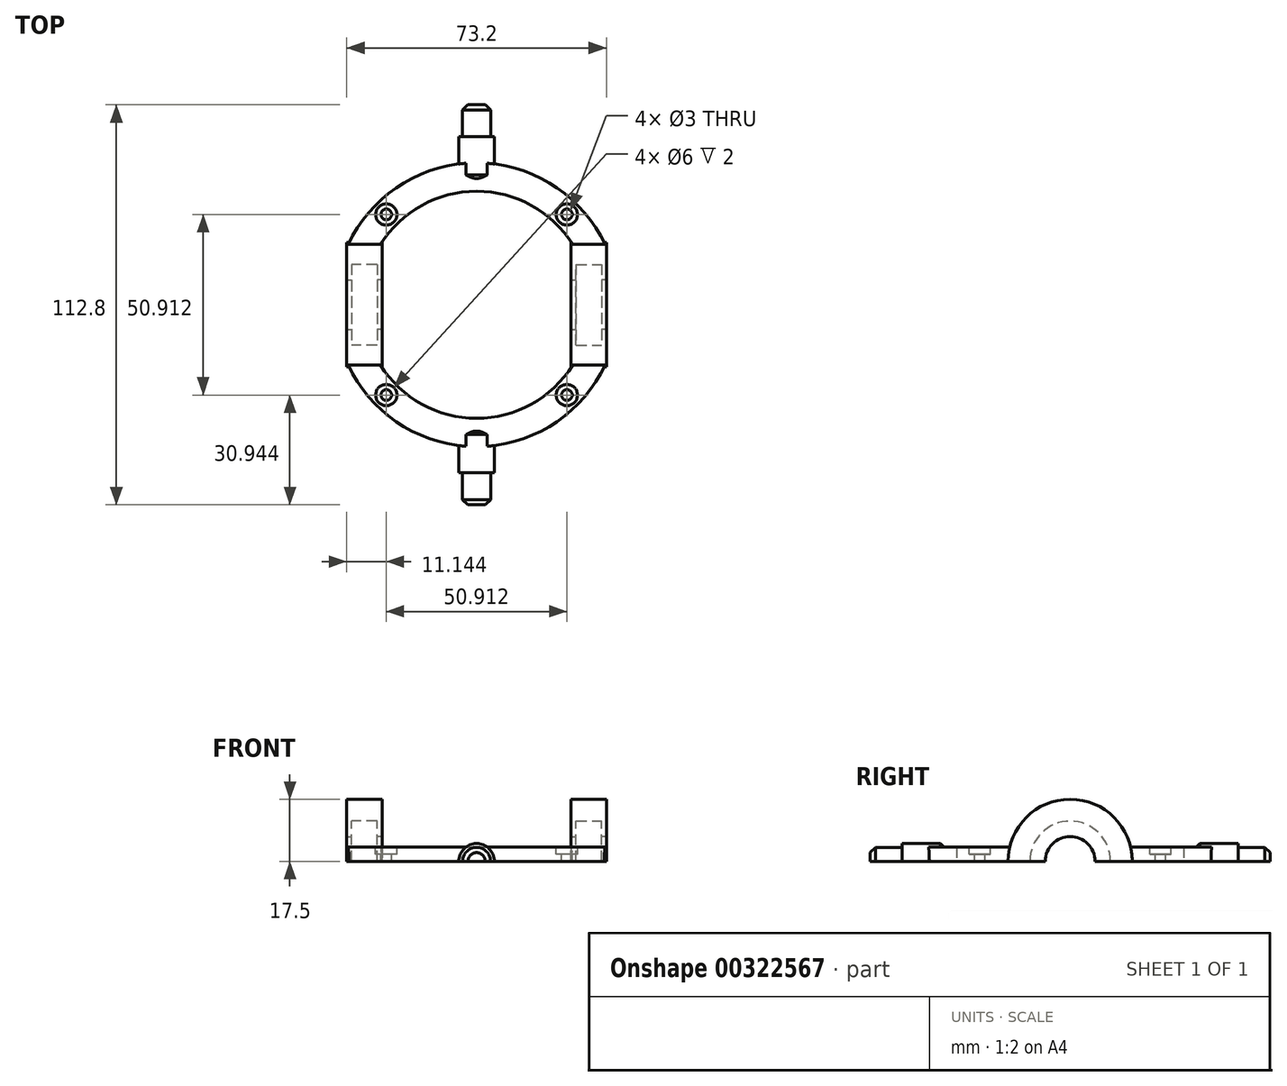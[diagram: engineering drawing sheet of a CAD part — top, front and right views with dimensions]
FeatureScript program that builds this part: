
annotation { "Feature Type Name" : "Feature", "Feature Type Description" : "" }
export const myFeature = defineFeature(function(context is Context, id is Id, definition is map)
    precondition{}
    {
        {
            var Q0;
            Q0=qCreatedBy(makeId("Top.planeOp"),FACE);
            var sketch = newSketch(context, id + "F0", { "sketchPlane" : qUnion([Q0])});
            skCircle(sketch, "E0", {"center": v(0, 0) * mm, "radius": 50 * mm});
            skCircle(sketch, "E1", {"center": v(0, 0) * mm, "radius": 58 * mm});
            skSolve(sketch);
        }
        {
            var Q0;
            Q0=qSketchRegion(id+"F0",true);
            extrude(context, id + "F1", {"entities" : qUnion([Q0]), "depth" : 4 * mm, "hasSecondDirection" : true, "secondDirectionOppositeDirection" : true, "secondDirectionDepth" : 4 * mm});
        }
        {
            var Q0;
            Q0=qCreatedBy(makeId("Front.planeOp"),FACE);
            cPlane(context, id + "F2", {"entities" : qUnion([Q0]), "cplaneType" : CPlaneType.OFFSET, "offset" : 54.8 * mm, "width" : 150 * mm, "height" : 150 * mm});
        }
        {
            var Q0;
            Q0=qCreatedBy(id+"F2.planeOp",FACE);
            var sketch = newSketch(context, id + "F3", { "sketchPlane" : qUnion([Q0])});
            skCircle(sketch, "E2", {"center": v(0, 0) * mm, "radius": 11.35 * mm});
            skCircle(sketch, "E3", {"center": v(0, 0) * mm, "radius": 17.5 * mm});
            skSolve(sketch);
        }
        {
            var Q0;
            Q0=makeQuery(id+"F3.imprint","IMPRINT",FACE,{"disambiguationData":[TD([[makeQuery(id+"F3.imprint","IMPRINT",EDGE,{"derivedFrom":sQuery(id+"F3.wireOp",EDGE,"E2")}),1.0]])]});
            var Q1;
            Q1=makeQuery(id+"F3.imprint","IMPRINT",FACE,{"disambiguationData":[TD([[makeQuery(id+"F3.imprint","IMPRINT",EDGE,{"derivedFrom":sQuery(id+"F3.wireOp",EDGE,"E2")}),-1.0]])]});
            extrude(context, id + "F4", {"entities" : qUnion([Q0, Q1]), "operationType" : NewBodyOperationType.REMOVE, "oppositeDirection" : true, "depth" : 25 * mm, "hasSecondDirection" : true, "secondDirectionOppositeDirection" : false, "secondDirectionDepth" : 25 * mm});
        }
        {
            var Q0;
            Q0=makeQuery(id+"F3.imprint","IMPRINT",FACE,{"disambiguationData":[TD([[makeQuery(id+"F3.imprint","IMPRINT",EDGE,{"derivedFrom":sQuery(id+"F3.wireOp",EDGE,"E2")}),-1.0]])]});
            extrude(context, id + "F5", {"entities" : qUnion([Q0]), "operationType" : NewBodyOperationType.ADD, "oppositeDirection" : true, "depth" : 7.2 * mm});
        }
        {
            var Q0;
            Q0=makeQuery(id+"F5.opExtrude","CAP_FACE",FACE,{"disambiguationData":[OSD([sQuery(id+"F3.wireOp",EDGE,"E2"),sQuery(id+"F3.wireOp",EDGE,"E3")])],"isStart":true});
            var sketch = newSketch(context, id + "F6", { "sketchPlane" : qUnion([Q0])});
            skCircle(sketch, "E4", {"center": v(0, 0) * mm, "radius": 7 * mm});
            skCircle(sketch, "E5", {"center": v(0, 0) * mm, "radius": 17.5 * mm});
            skSolve(sketch);
        }
        {
            var Q0;
            Q0=makeQuery(id+"F6.imprint","IMPRINT",FACE,{"disambiguationData":[TD([[makeQuery(id+"F6.imprint","IMPRINT",EDGE,{"derivedFrom":sQuery(id+"F6.wireOp",EDGE,"E4")}),-1.0]])]});
            var Q1;
            Q1=makeQuery(id+"F6.imprint","IMPRINT",FACE,{"disambiguationData":[TD([[makeQuery(id+"F6.imprint","IMPRINT",EDGE,{"derivedFrom":sQuery(id+"F6.wireOp",EDGE,"E5")}),1.0]])]});
            extrude(context, id + "F7", {"entities" : qUnion([Q0, Q1]), "operationType" : NewBodyOperationType.ADD, "depth" : 1.4 * mm});
        }
        {
            var Q0;
            Q0=makeQuery(id+"F5.opExtrude","CAP_FACE",FACE,{"disambiguationData":[OSD([sQuery(id+"F3.wireOp",EDGE,"E2"),sQuery(id+"F3.wireOp",EDGE,"E3")])],"isStart":false});
            var sketch = newSketch(context, id + "F8", { "sketchPlane" : qUnion([Q0])});
            skCircle(sketch, "E6", {"center": v(0, 0) * mm, "radius": 7 * mm});
            skCircle(sketch, "E7", {"center": v(0, 0) * mm, "radius": 17.5 * mm});
            skSolve(sketch);
        }
        {
            var Q0;
            Q0=makeQuery(id+"F8.imprint","IMPRINT",FACE,{"disambiguationData":[TD([[makeQuery(id+"F8.imprint","IMPRINT",EDGE,{"derivedFrom":sQuery(id+"F8.wireOp",EDGE,"E7")}),-1.0]])]});
            var Q1;
            Q1=makeQuery(id+"F8.imprint","IMPRINT",FACE,{"disambiguationData":[TD([[makeQuery(id+"F8.imprint","IMPRINT",EDGE,{"derivedFrom":sQuery(id+"F8.wireOp",EDGE,"E6")}),-1.0]])]});
            extrude(context, id + "F9", {"entities" : qUnion([Q0, Q1]), "operationType" : NewBodyOperationType.ADD, "depth" : 1.4 * mm});
        }
        {
            var Q0;
            Q0=qCreatedBy(makeId("Front.planeOp"),FACE);
            cPlane(context, id + "F10", {"entities" : qUnion([Q0]), "cplaneType" : CPlaneType.OFFSET, "offset" : 54.8 * mm, "oppositeDirection" : true, "width" : 150 * mm, "height" : 150 * mm});
        }
        {
            var Q0;
            Q0=qCreatedBy(id+"F10.planeOp",FACE);
            var sketch = newSketch(context, id + "F11", { "sketchPlane" : qUnion([Q0])});
            skCircle(sketch, "E8", {"center": v(0, 0) * mm, "radius": 17.5 * mm});
            skCircle(sketch, "E9", {"center": v(0, 0) * mm, "radius": 11.35 * mm});
            skSolve(sketch);
        }
        {
            var Q0;
            Q0=makeQuery(id+"F11.imprint","IMPRINT",FACE,{"disambiguationData":[TD([[makeQuery(id+"F11.imprint","IMPRINT",EDGE,{"derivedFrom":sQuery(id+"F11.wireOp",EDGE,"E8")}),1.0]])]});
            var Q1;
            Q1=makeQuery(id+"F11.imprint","IMPRINT",FACE,{"disambiguationData":[TD([[makeQuery(id+"F11.imprint","IMPRINT",EDGE,{"derivedFrom":sQuery(id+"F11.wireOp",EDGE,"E9")}),1.0]])]});
            extrude(context, id + "F12", {"entities" : qUnion([Q0, Q1]), "operationType" : NewBodyOperationType.REMOVE, "depth" : 25 * mm, "hasSecondDirection" : true, "secondDirectionOppositeDirection" : true, "secondDirectionDepth" : 25 * mm});
        }
        {
            var Q0;
            Q0=makeQuery(id+"F11.imprint","IMPRINT",FACE,{"disambiguationData":[TD([[makeQuery(id+"F11.imprint","IMPRINT",EDGE,{"derivedFrom":sQuery(id+"F11.wireOp",EDGE,"E8")}),1.0]])]});
            extrude(context, id + "F13", {"entities" : qUnion([Q0]), "operationType" : NewBodyOperationType.ADD, "depth" : 7.2 * mm});
        }
        {
            var Q0;
            Q0=makeQuery(id+"F13.opExtrude","CAP_FACE",FACE,{"disambiguationData":[OSD([sQuery(id+"F11.wireOp",EDGE,"E8"),sQuery(id+"F11.wireOp",EDGE,"E9")])],"isStart":true});
            var sketch = newSketch(context, id + "F14", { "sketchPlane" : qUnion([Q0])});
            skCircle(sketch, "E10", {"center": v(0, 0) * mm, "radius": 7 * mm});
            skCircle(sketch, "E11", {"center": v(0, 0) * mm, "radius": 17.5 * mm});
            skSolve(sketch);
        }
        {
            var Q0;
            Q0=makeQuery(id+"F14.imprint","IMPRINT",FACE,{"disambiguationData":[TD([[makeQuery(id+"F14.imprint","IMPRINT",EDGE,{"derivedFrom":makeQuery(id+"F13.opExtrude","CAP_EDGE",EDGE,{"disambiguationData":[OSD([sQuery(id+"F11.wireOp",EDGE,"E9")])],"isStart":true})}),1.0]])]});
            var Q1;
            Q1=makeQuery(id+"F14.imprint","IMPRINT",FACE,{"disambiguationData":[TD([[makeQuery(id+"F14.imprint","IMPRINT",EDGE,{"derivedFrom":sQuery(id+"F14.wireOp",EDGE,"E10")}),-1.0]])]});
            extrude(context, id + "F15", {"entities" : qUnion([Q0, Q1]), "operationType" : NewBodyOperationType.ADD, "depth" : 1.4 * mm});
        }
        {
            var Q0;
            Q0=makeQuery(id+"F13.opExtrude","CAP_FACE",FACE,{"disambiguationData":[OSD([sQuery(id+"F11.wireOp",EDGE,"E8"),sQuery(id+"F11.wireOp",EDGE,"E9")])],"isStart":false});
            var sketch = newSketch(context, id + "F16", { "sketchPlane" : qUnion([Q0])});
            skCircle(sketch, "E12", {"center": v(0, 0) * mm, "radius": 7 * mm});
            skCircle(sketch, "E13", {"center": v(0, 0) * mm, "radius": 17.5 * mm});
            skSolve(sketch);
        }
        {
            var Q0;
            Q0=makeQuery(id+"F16.imprint","IMPRINT",FACE,{"disambiguationData":[TD([[makeQuery(id+"F16.imprint","IMPRINT",EDGE,{"derivedFrom":sQuery(id+"F16.wireOp",EDGE,"E12")}),-1.0]])]});
            var Q1;
            Q1=makeQuery(id+"F16.imprint","IMPRINT",FACE,{"disambiguationData":[TD([[makeQuery(id+"F16.imprint","IMPRINT",EDGE,{"derivedFrom":sQuery(id+"F16.wireOp",EDGE,"E13")}),1.0]])]});
            extrude(context, id + "F17", {"entities" : qUnion([Q0, Q1]), "operationType" : NewBodyOperationType.ADD, "depth" : 1.4 * mm});
        }
        {
            var Q0;
            Q0=makeQuery(id+"F12.boolean.opBoolean","SPLIT",FACE,{"disambiguationData":[OD(0.0)],"derivedFrom":makeQuery(id+"F1.opExtrude","CAP_FACE",FACE,{"disambiguationData":[OSD([sQuery(id+"F0.wireOp",EDGE,"E0"),sQuery(id+"F0.wireOp",EDGE,"E1")])],"isStart":false})});
            var sketch = newSketch(context, id + "F18", { "sketchPlane" : qUnion([Q0])});
            skLineSegment(sketch, "E14", {"start": v(0, 0) * mm, "end": v(-50, 0) * mm, "construction": true});
            skLineSegment(sketch, "E15", {"start": v(-50, 0) * mm, "end": v(-58, 0) * mm, "construction": true});
            skCircle(sketch, "E16", {"center": v(-54, 0) * mm, "radius": 3 * mm});
            skCircle(sketch, "E17", {"center": v(-54, 0) * mm, "radius": 1.5 * mm});
            skCircle(sketch, "E18", {"center": v(-54, 0) * mm, "radius": 1 * mm});
            skCircle(sketch, "E19.1.0", {"center": v(-27, -46.77) * mm, "radius": 3 * mm});
            skCircle(sketch, "E19.1.1", {"center": v(-27, -46.77) * mm, "radius": 1.5 * mm});
            skCircle(sketch, "E19.1.2", {"center": v(-27, -46.77) * mm, "radius": 1 * mm});
            skCircle(sketch, "E19.2.0", {"center": v(27, -46.77) * mm, "radius": 3 * mm});
            skCircle(sketch, "E19.2.1", {"center": v(27, -46.77) * mm, "radius": 1.5 * mm});
            skCircle(sketch, "E19.2.2", {"center": v(27, -46.77) * mm, "radius": 1 * mm});
            skCircle(sketch, "E19.3.0", {"center": v(54, 0) * mm, "radius": 3 * mm});
            skCircle(sketch, "E19.3.1", {"center": v(54, 0) * mm, "radius": 1.5 * mm});
            skCircle(sketch, "E19.3.2", {"center": v(54, 0) * mm, "radius": 1 * mm});
            skCircle(sketch, "E19.4.0", {"center": v(27, 46.77) * mm, "radius": 3 * mm});
            skCircle(sketch, "E19.4.1", {"center": v(27, 46.77) * mm, "radius": 1.5 * mm});
            skCircle(sketch, "E19.4.2", {"center": v(27, 46.77) * mm, "radius": 1 * mm});
            skCircle(sketch, "E19.5.0", {"center": v(-27, 46.77) * mm, "radius": 3 * mm});
            skCircle(sketch, "E19.5.1", {"center": v(-27, 46.77) * mm, "radius": 1.5 * mm});
            skCircle(sketch, "E19.5.2", {"center": v(-27, 46.77) * mm, "radius": 1 * mm});
            skPoint(sketch, "E19.center", {"position": v(0, 0) * mm});
            skSolve(sketch);
        }
        {
            var Q0;
            Q0=makeQuery(id+"F18.imprint","IMPRINT",FACE,{"disambiguationData":[TD([[makeQuery(id+"F18.imprint","IMPRINT",EDGE,{"derivedFrom":sQuery(id+"F18.wireOp",EDGE,"E18")}),1.0]])]});
            var Q1;
            Q1=makeQuery(id+"F18.imprint","IMPRINT",FACE,{"disambiguationData":[TD([[makeQuery(id+"F18.imprint","IMPRINT",EDGE,{"derivedFrom":sQuery(id+"F18.wireOp",EDGE,"E19.5.2")}),1.0]])]});
            var Q2;
            Q2=makeQuery(id+"F18.imprint","IMPRINT",FACE,{"disambiguationData":[TD([[makeQuery(id+"F18.imprint","IMPRINT",EDGE,{"derivedFrom":sQuery(id+"F18.wireOp",EDGE,"E19.4.2")}),1.0]])]});
            var Q3;
            Q3=makeQuery(id+"F18.imprint","IMPRINT",FACE,{"disambiguationData":[TD([[makeQuery(id+"F18.imprint","IMPRINT",EDGE,{"derivedFrom":sQuery(id+"F18.wireOp",EDGE,"E19.3.2")}),1.0]])]});
            var Q4;
            Q4=makeQuery(id+"F18.imprint","IMPRINT",FACE,{"disambiguationData":[TD([[makeQuery(id+"F18.imprint","IMPRINT",EDGE,{"derivedFrom":sQuery(id+"F18.wireOp",EDGE,"E19.2.2")}),1.0]])]});
            var Q5;
            Q5=makeQuery(id+"F18.imprint","IMPRINT",FACE,{"disambiguationData":[TD([[makeQuery(id+"F18.imprint","IMPRINT",EDGE,{"derivedFrom":sQuery(id+"F18.wireOp",EDGE,"E19.1.2")}),1.0]])]});
            extrude(context, id + "F19", {"entities" : qUnion([Q0, Q1, Q2, Q3, Q4, Q5]), "operationType" : NewBodyOperationType.REMOVE, "oppositeDirection" : true, "depth" : 25 * mm});
        }
        {
            var Q0;
            Q0=makeQuery(id+"F18.imprint","IMPRINT",FACE,{"disambiguationData":[TD([[makeQuery(id+"F18.imprint","IMPRINT",EDGE,{"derivedFrom":sQuery(id+"F18.wireOp",EDGE,"E17")}),1.0]])]});
            var Q1;
            Q1=makeQuery(id+"F18.imprint","IMPRINT",FACE,{"disambiguationData":[TD([[makeQuery(id+"F18.imprint","IMPRINT",EDGE,{"derivedFrom":sQuery(id+"F18.wireOp",EDGE,"E19.5.1")}),1.0]])]});
            var Q2;
            Q2=makeQuery(id+"F18.imprint","IMPRINT",FACE,{"disambiguationData":[TD([[makeQuery(id+"F18.imprint","IMPRINT",EDGE,{"derivedFrom":sQuery(id+"F18.wireOp",EDGE,"E19.4.1")}),1.0]])]});
            var Q3;
            Q3=makeQuery(id+"F18.imprint","IMPRINT",FACE,{"disambiguationData":[TD([[makeQuery(id+"F18.imprint","IMPRINT",EDGE,{"derivedFrom":sQuery(id+"F18.wireOp",EDGE,"E19.3.1")}),1.0]])]});
            var Q4;
            Q4=makeQuery(id+"F18.imprint","IMPRINT",FACE,{"disambiguationData":[TD([[makeQuery(id+"F18.imprint","IMPRINT",EDGE,{"derivedFrom":sQuery(id+"F18.wireOp",EDGE,"E19.2.1")}),1.0]])]});
            var Q5;
            Q5=makeQuery(id+"F18.imprint","IMPRINT",FACE,{"disambiguationData":[TD([[makeQuery(id+"F18.imprint","IMPRINT",EDGE,{"derivedFrom":sQuery(id+"F18.wireOp",EDGE,"E19.1.1")}),1.0]])]});
            extrude(context, id + "F20", {"entities" : qUnion([Q0, Q1, Q2, Q3, Q4, Q5]), "operationType" : NewBodyOperationType.REMOVE, "oppositeDirection" : true, "depth" : 4 * mm});
        }
        {
            var Q0;
            Q0=makeQuery(id+"F18.imprint","IMPRINT",FACE,{"disambiguationData":[TD([[makeQuery(id+"F18.imprint","IMPRINT",EDGE,{"derivedFrom":sQuery(id+"F18.wireOp",EDGE,"E16")}),1.0]])]});
            var Q1;
            Q1=makeQuery(id+"F18.imprint","IMPRINT",FACE,{"disambiguationData":[TD([[makeQuery(id+"F18.imprint","IMPRINT",EDGE,{"derivedFrom":sQuery(id+"F18.wireOp",EDGE,"E19.1.0")}),1.0]])]});
            var Q2;
            Q2=makeQuery(id+"F18.imprint","IMPRINT",FACE,{"disambiguationData":[TD([[makeQuery(id+"F18.imprint","IMPRINT",EDGE,{"derivedFrom":sQuery(id+"F18.wireOp",EDGE,"E19.2.0")}),1.0]])]});
            var Q3;
            Q3=makeQuery(id+"F18.imprint","IMPRINT",FACE,{"disambiguationData":[TD([[makeQuery(id+"F18.imprint","IMPRINT",EDGE,{"derivedFrom":sQuery(id+"F18.wireOp",EDGE,"E19.3.0")}),1.0]])]});
            var Q4;
            Q4=makeQuery(id+"F18.imprint","IMPRINT",FACE,{"disambiguationData":[TD([[makeQuery(id+"F18.imprint","IMPRINT",EDGE,{"derivedFrom":sQuery(id+"F18.wireOp",EDGE,"E19.4.0")}),1.0]])]});
            var Q5;
            Q5=makeQuery(id+"F18.imprint","IMPRINT",FACE,{"disambiguationData":[TD([[makeQuery(id+"F18.imprint","IMPRINT",EDGE,{"derivedFrom":sQuery(id+"F18.wireOp",EDGE,"E19.5.0")}),1.0]])]});
            extrude(context, id + "F21", {"entities" : qUnion([Q0, Q1, Q2, Q3, Q4, Q5]), "operationType" : NewBodyOperationType.REMOVE, "oppositeDirection" : true, "depth" : 2 * mm});
        }
        {
            var Q0;
            Q0=qCreatedBy(makeId("Top.planeOp"),FACE);
            var sketch = newSketch(context, id + "F22", { "sketchPlane" : qUnion([Q0])});
            skCircle(sketch, "E20", {"center": v(0, 0) * mm, "radius": 40 * mm});
            skCircle(sketch, "E21", {"center": v(0, 0) * mm, "radius": 32 * mm});
            skSolve(sketch);
        }
        {
            var Q0;
            Q0 = qSketchRegion(id + "F22", true);
            extrude(context, id + "F23", {"entities" : qUnion([Q0]), "depth" : 4 * mm, "hasSecondDirection" : true, "secondDirectionOppositeDirection" : true, "secondDirectionDepth" : 4 * mm});
        }
        {
            var Q0;
            Q0=qCreatedBy(makeId("Front.planeOp"),FACE);
            cPlane(context, id + "F24", {"entities" : qUnion([Q0]), "cplaneType" : CPlaneType.OFFSET, "offset" : 35.2 * mm, "width" : 150 * mm, "height" : 150 * mm});
        }
        {
            var Q0;
            Q0=qCreatedBy(id+"F24.planeOp",FACE);
            var sketch = newSketch(context, id + "F25", { "sketchPlane" : qUnion([Q0])});
            skCircle(sketch, "E22.0", {"center": v(0, 0) * mm, "radius": 17.5 * mm});
            skCircle(sketch, "E23.0", {"center": v(0, 0) * mm, "radius": 11.35 * mm});
            skSolve(sketch);
        }
        {
            var Q0;
            Q0=makeQuery(id+"F25.imprint","IMPRINT",FACE,{"disambiguationData":[TD([[makeQuery(id+"F25.imprint","IMPRINT",EDGE,{"derivedFrom":sQuery(id+"F25.wireOp",EDGE,"E22.0")}),1.0]])]});
            var Q1;
            Q1=makeQuery(id+"F25.imprint","IMPRINT",FACE,{"disambiguationData":[TD([[makeQuery(id+"F25.imprint","IMPRINT",EDGE,{"derivedFrom":sQuery(id+"F25.wireOp",EDGE,"E23.0")}),1.0]])]});
            extrude(context, id + "F26", {"entities" : qUnion([Q0, Q1]), "operationType" : NewBodyOperationType.REMOVE, "oppositeDirection" : true, "depth" : 13.4 * mm, "hasSecondDirection" : true, "secondDirectionOppositeDirection" : false, "secondDirectionDepth" : 6.7 * mm});
        }
        {
            var Q0;
            Q0=makeQuery(id+"F25.imprint","IMPRINT",FACE,{"disambiguationData":[TD([[makeQuery(id+"F25.imprint","IMPRINT",EDGE,{"derivedFrom":sQuery(id+"F25.wireOp",EDGE,"E22.0")}),1.0]])]});
            extrude(context, id + "F27", {"entities" : qUnion([Q0]), "operationType" : NewBodyOperationType.ADD, "oppositeDirection" : true, "depth" : 7.2 * mm});
        }
        {
            var Q0;
            Q0=makeQuery(id+"F27.opExtrude","CAP_FACE",FACE,{"disambiguationData":[OSD([sQuery(id+"F25.wireOp",EDGE,"E22.0"),sQuery(id+"F25.wireOp",EDGE,"E23.0")])],"isStart":false});
            var sketch = newSketch(context, id + "F28", { "sketchPlane" : qUnion([Q0])});
            skCircle(sketch, "E24.0", {"center": v(0, 0) * mm, "radius": 7 * mm});
            skCircle(sketch, "E24.1", {"center": v(0, 0) * mm, "radius": 17.5 * mm});
            skSolve(sketch);
        }
        {
            var Q0;
            Q0=makeQuery(id+"F28.imprint","IMPRINT",FACE,{"disambiguationData":[TD([[makeQuery(id+"F28.imprint","IMPRINT",EDGE,{"derivedFrom":makeQuery(id+"F27.opExtrude","CAP_EDGE",EDGE,{"disambiguationData":[OSD([sQuery(id+"F25.wireOp",EDGE,"E23.0")])],"isStart":false})}),1.0]])]});
            var Q1;
            Q1=makeQuery(id+"F28.imprint","IMPRINT",FACE,{"disambiguationData":[TD([[makeQuery(id+"F28.imprint","IMPRINT",EDGE,{"derivedFrom":sQuery(id+"F28.wireOp",EDGE,"E24.0")}),-1.0]])]});
            extrude(context, id + "F29", {"entities" : qUnion([Q0, Q1]), "operationType" : NewBodyOperationType.ADD, "depth" : 1.4 * mm});
        }
        {
            var Q0;
            Q0=makeQuery(id+"F27.opExtrude","CAP_FACE",FACE,{"disambiguationData":[OSD([sQuery(id+"F25.wireOp",EDGE,"E22.0"),sQuery(id+"F25.wireOp",EDGE,"E23.0")])],"isStart":true});
            var sketch = newSketch(context, id + "F30", { "sketchPlane" : qUnion([Q0])});
            skCircle(sketch, "E25.0", {"center": v(0, 0) * mm, "radius": 7 * mm});
            skCircle(sketch, "E25.1", {"center": v(0, 0) * mm, "radius": 17.5 * mm});
            skSolve(sketch);
        }
        {
            var Q0;
            Q0=makeQuery(id+"F30.imprint","IMPRINT",FACE,{"disambiguationData":[TD([[makeQuery(id+"F30.imprint","IMPRINT",EDGE,{"derivedFrom":sQuery(id+"F30.wireOp",EDGE,"E25.1")}),1.0]])]});
            var Q1;
            Q1=makeQuery(id+"F30.imprint","IMPRINT",FACE,{"disambiguationData":[TD([[makeQuery(id+"F30.imprint","IMPRINT",EDGE,{"derivedFrom":sQuery(id+"F30.wireOp",EDGE,"E25.0")}),-1.0]])]});
            extrude(context, id + "F31", {"entities" : qUnion([Q0, Q1]), "operationType" : NewBodyOperationType.ADD, "depth" : 1.4 * mm});
        }
        {
            var Q0;
            Q0=qCreatedBy(makeId("Front.planeOp"),FACE);
            cPlane(context, id + "F32", {"entities" : qUnion([Q0]), "cplaneType" : CPlaneType.OFFSET, "offset" : 35.2 * mm, "oppositeDirection" : true, "width" : 150 * mm, "height" : 150 * mm});
        }
        {
            var Q0;
            Q0=qCreatedBy(id+"F32.planeOp",FACE);
            var sketch = newSketch(context, id + "F33", { "sketchPlane" : qUnion([Q0])});
            skCircle(sketch, "E26.0", {"center": v(0, 0) * mm, "radius": 17.5 * mm});
            skCircle(sketch, "E26.1", {"center": v(0, 0) * mm, "radius": 11.35 * mm});
            skSolve(sketch);
        }
        {
            var Q0;
            Q0=makeQuery(id+"F33.imprint","IMPRINT",FACE,{"disambiguationData":[TD([[makeQuery(id+"F33.imprint","IMPRINT",EDGE,{"derivedFrom":sQuery(id+"F33.wireOp",EDGE,"E26.0")}),1.0]])]});
            var Q1;
            Q1=makeQuery(id+"F33.imprint","IMPRINT",FACE,{"disambiguationData":[TD([[makeQuery(id+"F33.imprint","IMPRINT",EDGE,{"derivedFrom":sQuery(id+"F33.wireOp",EDGE,"E26.1")}),1.0]])]});
            extrude(context, id + "F34", {"entities" : qUnion([Q0, Q1]), "operationType" : NewBodyOperationType.REMOVE, "oppositeDirection" : true, "depth" : 7.2 * mm, "hasSecondDirection" : true, "secondDirectionOppositeDirection" : false, "secondDirectionDepth" : 25 * mm});
        }
        {
            var Q0;
            Q0=makeQuery(id+"F33.imprint","IMPRINT",FACE,{"disambiguationData":[TD([[makeQuery(id+"F33.imprint","IMPRINT",EDGE,{"derivedFrom":sQuery(id+"F33.wireOp",EDGE,"E26.0")}),1.0]])]});
            extrude(context, id + "F35", {"entities" : qUnion([Q0]), "operationType" : NewBodyOperationType.ADD, "depth" : 7.2 * mm});
        }
        {
            var Q0;
            Q0=qCreatedBy(id+"F32.planeOp",FACE);
            var sketch = newSketch(context, id + "F36", { "sketchPlane" : qUnion([Q0])});
            skCircle(sketch, "E27.0", {"center": v(0, 0) * mm, "radius": 7 * mm});
            skCircle(sketch, "E27.1", {"center": v(0, 0) * mm, "radius": 17.5 * mm});
            skSolve(sketch);
        }
        {
            var Q0;
            Q0=makeQuery(id+"F36.imprint","IMPRINT",FACE,{"disambiguationData":[TD([[makeQuery(id+"F36.imprint","IMPRINT",EDGE,{"derivedFrom":sQuery(id+"F36.wireOp",EDGE,"E27.0")}),-1.0]])]});
            extrude(context, id + "F37", {"entities" : qUnion([Q0]), "operationType" : NewBodyOperationType.ADD, "oppositeDirection" : true, "depth" : 1.4 * mm});
        }
        {
            var Q0;
            Q0=makeQuery(id+"F35.opExtrude","CAP_FACE",FACE,{"disambiguationData":[OSD([sQuery(id+"F33.wireOp",EDGE,"E26.0"),sQuery(id+"F33.wireOp",EDGE,"E26.1")])],"isStart":false});
            var sketch = newSketch(context, id + "F38", { "sketchPlane" : qUnion([Q0])});
            skCircle(sketch, "E28.0", {"center": v(0, 0) * mm, "radius": 7 * mm});
            skCircle(sketch, "E28.1", {"center": v(0, 0) * mm, "radius": 17.5 * mm});
            skSolve(sketch);
        }
        {
            var Q0;
            Q0=makeQuery(id+"F38.imprint","IMPRINT",FACE,{"disambiguationData":[TD([[makeQuery(id+"F38.imprint","IMPRINT",EDGE,{"derivedFrom":sQuery(id+"F38.wireOp",EDGE,"E28.0")}),-1.0]])]});
            var Q1;
            Q1=makeQuery(id+"F38.imprint","IMPRINT",FACE,{"disambiguationData":[TD([[makeQuery(id+"F38.imprint","IMPRINT",EDGE,{"derivedFrom":makeQuery(id+"F35.opExtrude","CAP_EDGE",EDGE,{"disambiguationData":[OSD([sQuery(id+"F33.wireOp",EDGE,"E26.1")])],"isStart":false})}),-1.0]])]});
            extrude(context, id + "F39", {"entities" : qUnion([Q0, Q1]), "operationType" : NewBodyOperationType.ADD, "depth" : 1.4 * mm});
        }
        {
            var Q0;
            Q0=qCreatedBy(makeId("Front.planeOp"),FACE);
            var sketch = newSketch(context, id + "F40", { "sketchPlane" : qUnion([Q0])});
            skLineSegment(sketch, "E29", {"start": v(0, 0) * mm, "end": v(0, 51.05) * mm});
            skSolve(sketch);
        }
        {
            var Q0;
            Q0=makeQuery(id+"F23.opExtrude","SWEPT_BODY",BODY,{"disambiguationData":[OSD([sQuery(id+"F22.wireOp",EDGE,"E20"),sQuery(id+"F22.wireOp",EDGE,"E21")])]});
            var Q1;
            Q1=sQuery(id+"F40.wireOp",EDGE,"E29");
            transform(context, id + "F41", {"entities" : qUnion([Q0]), "transformType" : TransformType.ROTATION, "transformAxis" : qUnion([Q1]), "angle" : 90 * degree, "makeCopy" : false});
        }
        {
            var Q0;
            Q0=makeQuery(id+"F17.opExtrude","CAP_FACE",FACE,{"disambiguationData":[OSD([sQuery(id+"F16.wireOp",EDGE,"E12"),sQuery(id+"F16.wireOp",EDGE,"E13")])],"isStart":true});
            var sketch = newSketch(context, id + "F42", { "sketchPlane" : qUnion([Q0])});
            skCircle(sketch, "E30", {"center": v(0, 0) * mm, "radius": 5 * mm});
            skSolve(sketch);
        }
        {
            var Q0;
            Q0 = qSketchRegion(id + "F42", true);
            extrude(context, id + "F43", {"entities" : qUnion([Q0]), "operationType" : NewBodyOperationType.ADD, "oppositeDirection" : true, "depth" : 12 * mm, "hasSecondDirection" : true, "secondDirectionOppositeDirection" : false, "secondDirectionDepth" : -.2 * mm});
        }
        {
            var Q0;
            {var subQ0=sQuery(id+"F42.wireOp",EDGE,"E30");Q0=makeQuery(id+"F43.boolean.opBoolean","SPLIT",EDGE,{"disambiguationData":[TD([makeQuery(id+"F23.opExtrude","CAP_FACE",FACE,{"disambiguationData":[OSD([sQuery(id+"F22.wireOp",EDGE,"E20"),sQuery(id+"F22.wireOp",EDGE,"E21")])],"isStart":false})])],"derivedFrom":makeQuery(id+"F43.opExtrude","CAP_EDGE",EDGE,{"disambiguationData":[OSD([subQ0])],"isStart":false})});}
            var Q1;
            {var subQ0=sQuery(id+"F42.wireOp",EDGE,"E30");Q1=makeQuery(id+"F43.boolean.opBoolean","SPLIT",EDGE,{"disambiguationData":[TD([makeQuery(id+"F23.opExtrude","CAP_FACE",FACE,{"disambiguationData":[OSD([sQuery(id+"F22.wireOp",EDGE,"E20"),sQuery(id+"F22.wireOp",EDGE,"E21")])],"isStart":true})])],"derivedFrom":makeQuery(id+"F43.opExtrude","CAP_EDGE",EDGE,{"disambiguationData":[OSD([subQ0])],"isStart":false})});}
            chamfer(context, id + "F44", {"entities" : qUnion([Q0, Q1]), "width" : 1 * mm, "tangentPropagation" : true});
        }
        {
            var Q0;
            Q0=makeQuery(id+"F43.opExtrude","CAP_FACE",FACE,{"disambiguationData":[OSD([sQuery(id+"F42.wireOp",EDGE,"E30")])],"isStart":true});
            var sketch = newSketch(context, id + "F45", { "sketchPlane" : qUnion([Q0])});
            skCircle(sketch, "E31", {"center": v(0, 0) * mm, "radius": 3.95 * mm});
            skSolve(sketch);
        }
        {
            var Q0;
            Q0=makeQuery(id+"F45.imprint","IMPRINT",FACE,{"disambiguationData":[TD([[makeQuery(id+"F45.imprint","IMPRINT",EDGE,{"derivedFrom":sQuery(id+"F45.wireOp",EDGE,"E31")}),1.0]])]});
            extrude(context, id + "F46", {"entities" : qUnion([Q0]), "operationType" : NewBodyOperationType.ADD, "depth" : 9 * mm});
        }
        {
            var Q0;
            Q0=makeQuery(id+"F9.opExtrude","CAP_FACE",FACE,{"disambiguationData":[OSD([sQuery(id+"F8.wireOp",EDGE,"E6"),sQuery(id+"F8.wireOp",EDGE,"E7")])],"isStart":true});
            var sketch = newSketch(context, id + "F47", { "sketchPlane" : qUnion([Q0])});
            skCircle(sketch, "E32", {"center": v(0, 0) * mm, "radius": 5 * mm});
            skSolve(sketch);
        }
        {
            var Q0;
            Q0 = qSketchRegion(id + "F47", true);
            extrude(context, id + "F48", {"entities" : qUnion([Q0]), "operationType" : NewBodyOperationType.ADD, "oppositeDirection" : true, "depth" : 12 * mm, "hasSecondDirection" : true, "secondDirectionOppositeDirection" : false, "secondDirectionDepth" : -.2 * mm});
        }
        {
            var Q0;
            {var subQ0=sQuery(id+"F47.wireOp",EDGE,"E32");Q0=makeQuery(id+"F48.boolean.opBoolean","SPLIT",EDGE,{"disambiguationData":[TD([makeQuery(id+"F23.opExtrude","CAP_FACE",FACE,{"disambiguationData":[OSD([sQuery(id+"F22.wireOp",EDGE,"E20"),sQuery(id+"F22.wireOp",EDGE,"E21")])],"isStart":false})])],"derivedFrom":makeQuery(id+"F48.opExtrude","CAP_EDGE",EDGE,{"disambiguationData":[OSD([subQ0])],"isStart":false})});}
            var Q1;
            {var subQ0=sQuery(id+"F47.wireOp",EDGE,"E32");Q1=makeQuery(id+"F48.boolean.opBoolean","SPLIT",EDGE,{"disambiguationData":[TD([makeQuery(id+"F23.opExtrude","CAP_FACE",FACE,{"disambiguationData":[OSD([sQuery(id+"F22.wireOp",EDGE,"E20"),sQuery(id+"F22.wireOp",EDGE,"E21")])],"isStart":true})])],"derivedFrom":makeQuery(id+"F48.opExtrude","CAP_EDGE",EDGE,{"disambiguationData":[OSD([subQ0])],"isStart":false})});}
            chamfer(context, id + "F49", {"entities" : qUnion([Q0, Q1]), "width" : 1 * mm, "tangentPropagation" : true});
        }
        {
            var Q0;
            Q0=makeQuery(id+"F48.opExtrude","CAP_FACE",FACE,{"disambiguationData":[OSD([sQuery(id+"F47.wireOp",EDGE,"E32")])],"isStart":true});
            var sketch = newSketch(context, id + "F50", { "sketchPlane" : qUnion([Q0])});
            skCircle(sketch, "E33", {"center": v(0, 0) * mm, "radius": 3.95 * mm});
            skSolve(sketch);
        }
        {
            var Q0;
            Q0 = qSketchRegion(id + "F50", true);
            extrude(context, id + "F51", {"entities" : qUnion([Q0]), "operationType" : NewBodyOperationType.ADD, "depth" : 9 * mm});
        }
        {
            var Q0;
            Q0=makeQuery(id+"F51.opExtrude","CAP_EDGE",EDGE,{"disambiguationData":[OSD([sQuery(id+"F50.wireOp",EDGE,"E33")])],"isStart":false});
            var Q1;
            Q1=makeQuery(id+"F46.opExtrude","CAP_EDGE",EDGE,{"disambiguationData":[OSD([sQuery(id+"F45.wireOp",EDGE,"E31")])],"isStart":false});
            chamfer(context, id + "F52", {"entities" : qUnion([Q0, Q1]), "width" : 1.5 * mm, "tangentPropagation" : true});
        }
        {
            var Q0;
            Q0=makeQuery(id+"F1.opExtrude","SWEPT_BODY",BODY,{"disambiguationData":[OSD([sQuery(id+"F0.wireOp",EDGE,"E0"),sQuery(id+"F0.wireOp",EDGE,"E1")])]});
            deleteBodies(context, id + "F53", {"entities" : qUnion([Q0])});
        }
        {
            var Q0;
            Q0=makeQuery(id+"F34.boolean.opBoolean","SPLIT",FACE,{"disambiguationData":[OD(1.0)],"derivedFrom":makeQuery(id+"F23.opExtrude","CAP_FACE",FACE,{"disambiguationData":[OSD([sQuery(id+"F22.wireOp",EDGE,"E20"),sQuery(id+"F22.wireOp",EDGE,"E21")])],"isStart":false})});
            var sketch = newSketch(context, id + "F54", { "sketchPlane" : qUnion([Q0])});
            skLineSegment(sketch, "E34", {"start": v(0, 0) * mm, "end": v(-25.46, 25.46) * mm, "construction": true});
            skCircle(sketch, "E35", {"center": v(-25.46, 25.46) * mm, "radius": 3 * mm});
            skCircle(sketch, "E36", {"center": v(-25.46, 25.46) * mm, "radius": 1.5 * mm});
            skCircle(sketch, "E37", {"center": v(-25.46, 25.46) * mm, "radius": 1 * mm});
            skCircle(sketch, "E38.1.0", {"center": v(-25.46, -25.46) * mm, "radius": 3 * mm});
            skCircle(sketch, "E38.1.1", {"center": v(-25.46, -25.46) * mm, "radius": 1.5 * mm});
            skCircle(sketch, "E38.1.2", {"center": v(-25.46, -25.46) * mm, "radius": 1 * mm});
            skCircle(sketch, "E38.2.0", {"center": v(25.46, -25.46) * mm, "radius": 3 * mm});
            skCircle(sketch, "E38.2.1", {"center": v(25.46, -25.46) * mm, "radius": 1.5 * mm});
            skCircle(sketch, "E38.2.2", {"center": v(25.46, -25.46) * mm, "radius": 1 * mm});
            skCircle(sketch, "E38.3.0", {"center": v(25.46, 25.46) * mm, "radius": 3 * mm});
            skCircle(sketch, "E38.3.1", {"center": v(25.46, 25.46) * mm, "radius": 1.5 * mm});
            skCircle(sketch, "E38.3.2", {"center": v(25.46, 25.46) * mm, "radius": 1 * mm});
            skPoint(sketch, "E38.center", {"position": v(0, 0) * mm});
            skSolve(sketch);
        }
        {
            var Q0;
            Q0=makeQuery(id+"F54.imprint","IMPRINT",FACE,{"disambiguationData":[TD([[makeQuery(id+"F54.imprint","IMPRINT",EDGE,{"derivedFrom":sQuery(id+"F54.wireOp",EDGE,"E37")}),1.0]])]});
            var Q1;
            Q1=makeQuery(id+"F54.imprint","IMPRINT",FACE,{"disambiguationData":[TD([[makeQuery(id+"F54.imprint","IMPRINT",EDGE,{"derivedFrom":sQuery(id+"F54.wireOp",EDGE,"E38.3.2")}),1.0]])]});
            var Q2;
            Q2=makeQuery(id+"F54.imprint","IMPRINT",FACE,{"disambiguationData":[TD([[makeQuery(id+"F54.imprint","IMPRINT",EDGE,{"derivedFrom":sQuery(id+"F54.wireOp",EDGE,"E38.2.2")}),1.0]])]});
            var Q3;
            Q3=makeQuery(id+"F54.imprint","IMPRINT",FACE,{"disambiguationData":[TD([[makeQuery(id+"F54.imprint","IMPRINT",EDGE,{"derivedFrom":sQuery(id+"F54.wireOp",EDGE,"E38.1.2")}),1.0]])]});
            extrude(context, id + "F55", {"entities" : qUnion([Q0, Q1, Q2, Q3]), "operationType" : NewBodyOperationType.REMOVE, "oppositeDirection" : true, "depth" : 25 * mm});
        }
        {
            var Q0;
            Q0=makeQuery(id+"F54.imprint","IMPRINT",FACE,{"disambiguationData":[TD([[makeQuery(id+"F54.imprint","IMPRINT",EDGE,{"derivedFrom":sQuery(id+"F54.wireOp",EDGE,"E36")}),1.0]])]});
            var Q1;
            Q1=makeQuery(id+"F54.imprint","IMPRINT",FACE,{"disambiguationData":[TD([[makeQuery(id+"F54.imprint","IMPRINT",EDGE,{"derivedFrom":sQuery(id+"F54.wireOp",EDGE,"E38.3.1")}),1.0]])]});
            var Q2;
            Q2=makeQuery(id+"F54.imprint","IMPRINT",FACE,{"disambiguationData":[TD([[makeQuery(id+"F54.imprint","IMPRINT",EDGE,{"derivedFrom":sQuery(id+"F54.wireOp",EDGE,"E38.2.1")}),1.0]])]});
            var Q3;
            Q3=makeQuery(id+"F54.imprint","IMPRINT",FACE,{"disambiguationData":[TD([[makeQuery(id+"F54.imprint","IMPRINT",EDGE,{"derivedFrom":sQuery(id+"F54.wireOp",EDGE,"E38.1.1")}),1.0]])]});
            extrude(context, id + "F56", {"entities" : qUnion([Q0, Q1, Q2, Q3]), "operationType" : NewBodyOperationType.REMOVE, "oppositeDirection" : true, "depth" : 4 * mm});
        }
        {
            var Q0;
            Q0=makeQuery(id+"F54.imprint","IMPRINT",FACE,{"disambiguationData":[TD([[makeQuery(id+"F54.imprint","IMPRINT",EDGE,{"derivedFrom":sQuery(id+"F54.wireOp",EDGE,"E35")}),1.0]])]});
            var Q1;
            Q1=makeQuery(id+"F54.imprint","IMPRINT",FACE,{"disambiguationData":[TD([[makeQuery(id+"F54.imprint","IMPRINT",EDGE,{"derivedFrom":sQuery(id+"F54.wireOp",EDGE,"E38.3.0")}),1.0]])]});
            var Q2;
            Q2=makeQuery(id+"F54.imprint","IMPRINT",FACE,{"disambiguationData":[TD([[makeQuery(id+"F54.imprint","IMPRINT",EDGE,{"derivedFrom":sQuery(id+"F54.wireOp",EDGE,"E38.2.0")}),1.0]])]});
            var Q3;
            Q3=makeQuery(id+"F54.imprint","IMPRINT",FACE,{"disambiguationData":[TD([[makeQuery(id+"F54.imprint","IMPRINT",EDGE,{"derivedFrom":sQuery(id+"F54.wireOp",EDGE,"E38.1.0")}),1.0]])]});
            extrude(context, id + "F57", {"entities" : qUnion([Q0, Q1, Q2, Q3]), "operationType" : NewBodyOperationType.REMOVE, "oppositeDirection" : true, "depth" : 2 * mm});
        }
        {
            var Q0;
            Q0=qCreatedBy(makeId("Top.planeOp"),FACE);
            var sketch = newSketch(context, id + "F58", { "sketchPlane" : qUnion([Q0])});
            skCircle(sketch, "E39", {"center": v(0, 0) * mm, "radius": 67.8 * mm});
            skSolve(sketch);
        }
        {
            var Q0;
            Q0 = qSketchRegion(id + "F58", true);
            extrude(context, id + "F59", {"entities" : qUnion([Q0]), "operationType" : NewBodyOperationType.REMOVE, "oppositeDirection" : true, "depth" : 25 * mm});
        }
    });
